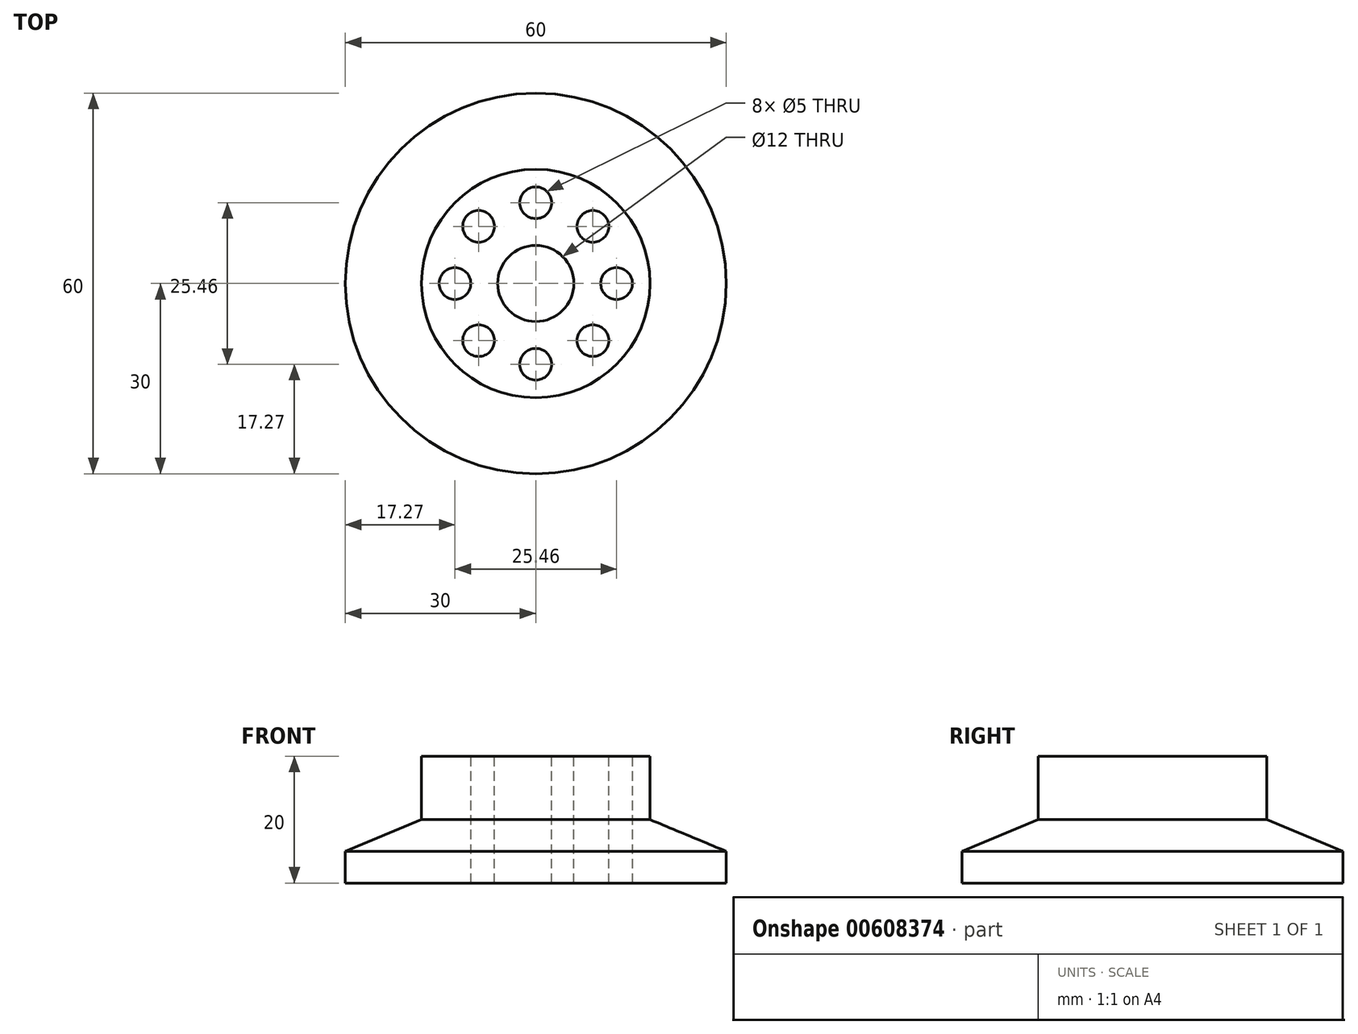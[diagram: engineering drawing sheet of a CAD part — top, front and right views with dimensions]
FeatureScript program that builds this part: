
annotation { "Feature Type Name" : "Feature", "Feature Type Description" : "" }
export const myFeature = defineFeature(function(context is Context, id is Id, definition is map)
    precondition{}
    {
        {
            var Q0;
            Q0=qCreatedBy(makeId("Top.planeOp"),FACE);
            var sketch = newSketch(context, id + "F0", { "sketchPlane" : qUnion([Q0])});
            skCircle(sketch, "E0", {"center": v(0, 0) * mm, "radius": 30 * mm});
            skSolve(sketch);
        }
        {
            var Q0;
            Q0=makeQuery(id+"F0.imprint","IMPRINT",FACE,{"disambiguationData":[TD([[makeQuery(id+"F0.imprint","IMPRINT",EDGE,{"derivedFrom":sQuery(id+"F0.wireOp",EDGE,"E0")}),1.0]])]});
            extrude(context, id + "F1", {"entities" : qUnion([Q0]), "depth" : 20 * mm, "offsetDistance" : 25 * mm});
        }
        {
            var Q0;
            Q0=makeQuery(id+"F1.opExtrude","CAP_EDGE",EDGE,{"disambiguationData":[OSD([sQuery(id+"F0.wireOp",EDGE,"E0")])],"isStart":false});
            chamfer(context, id + "F2", {"entities" : qUnion([Q0]), "chamferType" : ChamferType.TWO_OFFSETS, "width1" : 12 * mm, "oppositeDirection" : false, "width2" : 5 * mm, "tangentPropagation" : true});
        }
        {
            var Q0;
            Q0=makeQuery(id+"F1.opExtrude","CAP_FACE",FACE,{"disambiguationData":[OSD([sQuery(id+"F0.wireOp",EDGE,"E0")])],"isStart":false});
            extrude(context, id + "F3", {"entities" : qUnion([Q0]), "operationType" : NewBodyOperationType.ADD, "depth" : 20 * mm, "offsetDistance" : 25 * mm});
        }
        {
            var Q0;
            Q0=makeQuery(id+"F3.opExtrude","CAP_FACE",FACE,{"disambiguationData":[OSD([sQuery(id+"F0.wireOp",EDGE,"E0")])],"isStart":false});
            var sketch = newSketch(context, id + "F4", { "sketchPlane" : qUnion([Q0])});
            skCircle(sketch, "E1", {"center": v(0, 0) * mm, "radius": 6 * mm});
            skPoint(sketch, "E2", {"position": v(0, 12.73) * mm});
            skPoint(sketch, "E3", {"position": v(0, -12.73) * mm});
            skPoint(sketch, "E4", {"position": v(12.73, 0) * mm});
            skPoint(sketch, "E5", {"position": v(-12.73, 0) * mm});
            skCircle(sketch, "E6", {"center": v(-12.73, 0) * mm, "radius": 2.5 * mm});
            skCircle(sketch, "E7", {"center": v(0, 12.73) * mm, "radius": 2.5 * mm});
            skCircle(sketch, "E8", {"center": v(0, -12.73) * mm, "radius": 2.5 * mm});
            skCircle(sketch, "E9", {"center": v(12.73, 0) * mm, "radius": 2.5 * mm});
            skCircle(sketch, "E10", {"center": v(0, 12.73) * mm, "radius": 4 * mm});
            skCircle(sketch, "E11", {"center": v(-12.73, 0) * mm, "radius": 4 * mm});
            skCircle(sketch, "E12", {"center": v(0, -12.73) * mm, "radius": 4 * mm});
            skCircle(sketch, "E13", {"center": v(12.73, 0) * mm, "radius": 4 * mm});
            skLineSegment(sketch, "E14", {"start": v(-12.73, 0) * mm, "end": v(0, 12.73) * mm});
            skLineSegment(sketch, "E15", {"start": v(0, 12.73) * mm, "end": v(12.73, 0) * mm});
            skLineSegment(sketch, "E16", {"start": v(12.73, 0) * mm, "end": v(0, -12.73) * mm});
            skLineSegment(sketch, "E17", {"start": v(0, -12.73) * mm, "end": v(-12.73, 0) * mm});
            skLineSegment(sketch, "E18", {"start": v(0, 0) * mm, "end": v(9, 9) * mm});
            skLineSegment(sketch, "E19", {"start": v(0, 0) * mm, "end": v(-9, 9) * mm});
            skLineSegment(sketch, "E20", {"start": v(0, 0) * mm, "end": v(-9, -9) * mm});
            skLineSegment(sketch, "E21", {"start": v(0, 0) * mm, "end": v(9, -9) * mm});
            skCircle(sketch, "E22", {"center": v(-9, 9) * mm, "radius": 2.5 * mm});
            skCircle(sketch, "E23", {"center": v(-9, -9) * mm, "radius": 2.5 * mm});
            skCircle(sketch, "E24", {"center": v(9, -9) * mm, "radius": 2.5 * mm});
            skCircle(sketch, "E25", {"center": v(9, 9) * mm, "radius": 2.5 * mm});
            skSolve(sketch);
        }
        {
            var Q0;
            Q0=makeQuery(id+"F4.imprint","IMPRINT",FACE,{"disambiguationData":[TD([[makeQuery(id+"F4.imprint","IMPRINT",EDGE,{"derivedFrom":sQuery(id+"F4.wireOp",EDGE,"E6")}),1.0]])]});
            var Q1;
            Q1=makeQuery(id+"F4.imprint","IMPRINT",FACE,{"disambiguationData":[TD([[makeQuery(id+"F4.imprint","IMPRINT",EDGE,{"derivedFrom":sQuery(id+"F4.wireOp",EDGE,"E1")}),1.0]])]});
            var Q2;
            Q2=makeQuery(id+"F4.imprint","IMPRINT",FACE,{"disambiguationData":[TD([[makeQuery(id+"F4.imprint","IMPRINT",EDGE,{"derivedFrom":sQuery(id+"F4.wireOp",EDGE,"E7")}),1.0]])]});
            var Q3;
            Q3=makeQuery(id+"F4.imprint","IMPRINT",FACE,{"disambiguationData":[TD([[makeQuery(id+"F4.imprint","IMPRINT",EDGE,{"derivedFrom":sQuery(id+"F4.wireOp",EDGE,"E9")}),1.0]])]});
            var Q4;
            Q4=makeQuery(id+"F4.imprint","IMPRINT",FACE,{"disambiguationData":[TD([[makeQuery(id+"F4.imprint","IMPRINT",EDGE,{"derivedFrom":sQuery(id+"F4.wireOp",EDGE,"E8")}),1.0]])]});
            var Q5;
            Q5=makeQuery(id+"F4.imprint","IMPRINT",FACE,{"disambiguationData":[TD([[makeQuery(id+"F4.imprint","IMPRINT",EDGE,{"derivedFrom":sQuery(id+"F4.wireOp",EDGE,"E25")}),1.0]])]});
            var Q6;
            Q6=makeQuery(id+"F4.imprint","IMPRINT",FACE,{"disambiguationData":[TD([[makeQuery(id+"F4.imprint","IMPRINT",EDGE,{"derivedFrom":sQuery(id+"F4.wireOp",EDGE,"E22")}),1.0]])]});
            var Q7;
            Q7=makeQuery(id+"F4.imprint","IMPRINT",FACE,{"disambiguationData":[TD([[makeQuery(id+"F4.imprint","IMPRINT",EDGE,{"derivedFrom":sQuery(id+"F4.wireOp",EDGE,"E23")}),1.0]])]});
            var Q8;
            Q8=makeQuery(id+"F4.imprint","IMPRINT",FACE,{"disambiguationData":[TD([[makeQuery(id+"F4.imprint","IMPRINT",EDGE,{"derivedFrom":sQuery(id+"F4.wireOp",EDGE,"E24")}),1.0]])]});
            extrude(context, id + "F5", {"entities" : qUnion([Q0, Q1, Q2, Q3, Q4, Q5, Q6, Q7, Q8]), "operationType" : NewBodyOperationType.REMOVE, "oppositeDirection" : true, "depth" : 50 * mm, "offsetDistance" : 25 * mm});
        }
        {
            var Q0;
            Q0=makeQuery(id+"F3.opExtrude","CAP_FACE",FACE,{"disambiguationData":[OSD([sQuery(id+"F0.wireOp",EDGE,"E0")])],"isStart":false});
            extrude(context, id + "F6", {"entities" : qUnion([Q0]), "operationType" : NewBodyOperationType.REMOVE, "oppositeDirection" : true, "depth" : 10 * mm, "offsetDistance" : 25 * mm});
        }
        {
            var Q0;
            Q0=makeQuery(id+"F1.opExtrude","CAP_FACE",FACE,{"disambiguationData":[OSD([sQuery(id+"F0.wireOp",EDGE,"E0")])],"isStart":true});
            extrude(context, id + "F7", {"entities" : qUnion([Q0]), "operationType" : NewBodyOperationType.REMOVE, "oppositeDirection" : true, "depth" : 10 * mm, "offsetDistance" : 25 * mm});
        }
    });
